# Revit family: 609631001_Solid Asiento Sanitario
name_source: partatom
category: Plumbing Fixtures
units: mm (PartAtom-declared; Revit-internal decimal feet)

## family parameters
Always vertical = Yes
Cut with Voids When Loaded = No
OmniClass Number = 23.31.19.19.17
OmniClass Title = Water Closet Seats
Part Type = Normal
Room Calculation Point = No
Round Connector Dimension = Use Diameter
Shared = No
Work Plane-Based = No

## types (1)
- 609631001_Solid Asiento Sanitario
    Acabado = Natural pigmentado.
    Alto = 59 mm
    Ancho = 358 mm  [stored 1.17454 ft]
    Colección = Solid con Tapa
    Creado por = BIMBAU
    Default Elevation = 0 mm  [stored 0 ft]
    Description = Para la comodidad del usuario, debes adquirir este asiendo ergonómico con tapa de cierre suave. De mayor espesor y ancho del aro para un uso más confortable. Un producto de fácil instalación, limpieza y mantenimiento.
    Fecha de creación = 15/04/2021
    Garantía = 5 Años
    Línea = Asientos Institucionales
    Manufacturer = Corona
    Material = Corona_Plastico_Blanco
    Material 2 = Corona_Acero
    Model = Solid
    Peso Neto aprox = 1685 gr. - 3,71 lb.
    Profundidad = 478 mm  [stored 1.56824 ft]
    Rango de Ángulo de Detección = 0º - 95º.
    Referencia = 609631001
    Resistencia = Resistente a la corrosión pelado y decoloración por agua
    URL = https://corona.co
    Uso = Institucional
    Vida Útil de la Bisagra = 25.000 ciclos.

note: [stored X ft] marks values corroborated as IEEE doubles in the binary element streams (Revit-internal decimal feet)

## geometry (parser evidence)
native form markers: Sweep x3
no freeform markers — native parametric forms only
